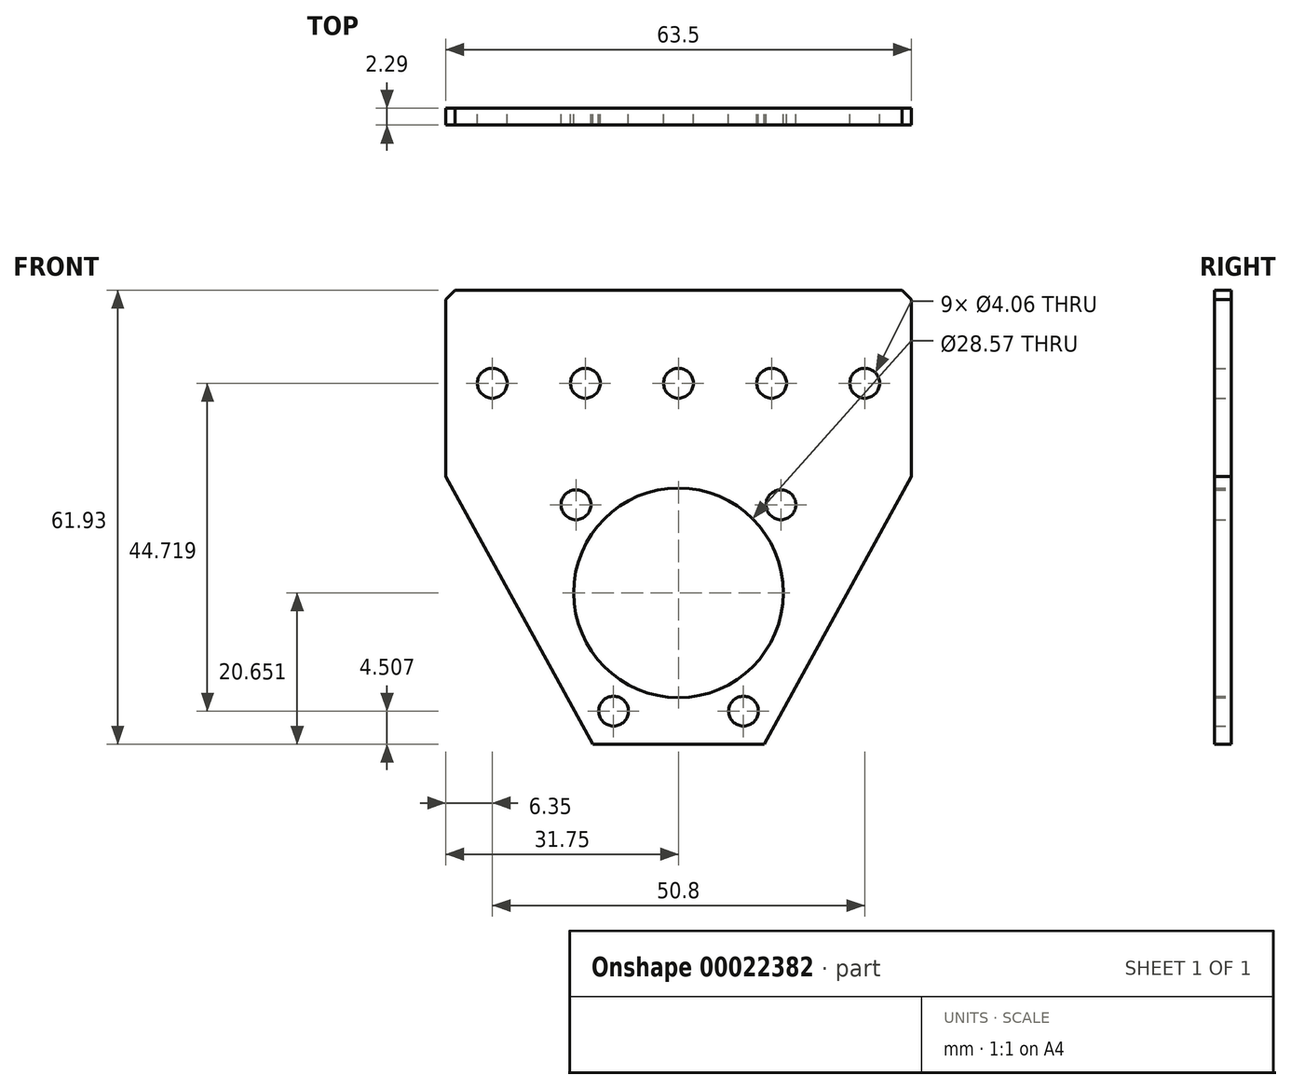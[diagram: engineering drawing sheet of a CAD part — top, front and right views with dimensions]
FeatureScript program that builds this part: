
annotation { "Feature Type Name" : "Feature", "Feature Type Description" : "" }
export const myFeature = defineFeature(function(context is Context, id is Id, definition is map)
    precondition{}
    {
        {
            var Q0;
            Q0=qCreatedBy(makeId("Front.planeOp"),FACE);
            var sketch = newSketch(context, id + "F0", { "sketchPlane" : qUnion([Q0])});
            skLineSegment(sketch, "E0.bottom", {"start": v(-31.75, 16.43) * mm, "end": v(31.75, 16.43) * mm});
            skLineSegment(sketch, "E0.top", {"start": v(-11.7, -45.5) * mm, "end": v(11.7, -45.5) * mm});
            skLineSegment(sketch, "E0.left", {"start": v(-31.75, 16.43) * mm, "end": v(-31.75, -8.97) * mm});
            skLineSegment(sketch, "E0.right", {"start": v(31.75, 16.43) * mm, "end": v(31.75, -8.97) * mm});
            skLineSegment(sketch, "E1", {"start": v(-31.75, -8.97) * mm, "end": v(-11.7, -45.5) * mm});
            skLineSegment(sketch, "E2", {"start": v(31.75, -8.97) * mm, "end": v(11.7, -45.5) * mm});
            skLineSegment(sketch, "E3", {"start": v(31.75, 3.73) * mm, "end": v(-31.75, 3.73) * mm, "construction": true});
            skCircle(sketch, "E4", {"center": v(0, -24.85) * mm, "radius": 14.29 * mm});
            skSolve(sketch);
        }
        {
            var Q0;
            Q0=makeQuery(id+"F0.imprint","IMPRINT",FACE,{"disambiguationData":[TD([[makeQuery(id+"F0.imprint","IMPRINT",EDGE,{"derivedFrom":sQuery(id+"F0.wireOp",EDGE,"E0.bottom")}),-1.0]])]});
            extrude(context, id + "F1", {"entities" : qUnion([Q0]), "depth" : 2.3 * mm});
        }
        {
            var Q0;
            Q0=makeQuery(id+"F1.opExtrude","CAP_FACE",FACE,{"disambiguationData":[OSD([sQuery(id+"F0.wireOp",EDGE,"E0.bottom"),sQuery(id+"F0.wireOp",EDGE,"E0.top"),sQuery(id+"F0.wireOp",EDGE,"E0.left"),sQuery(id+"F0.wireOp",EDGE,"E0.right"),sQuery(id+"F0.wireOp",EDGE,"dd962b13-b751-4e5a-9dd1-f75176092dec"),sQuery(id+"F0.wireOp",EDGE,"E1"),sQuery(id+"F0.wireOp",EDGE,"E2")])],"isStart":true});
            var sketch = newSketch(context, id + "F2", { "sketchPlane" : qUnion([Q0])});
            skLineSegment(sketch, "E5.bottom", {"start": v(-25.4, 3.73) * mm, "end": v(25.4, 3.73) * mm});
            skLineSegment(sketch, "E5.top", {"start": v(-25.4, -45.5) * mm, "end": v(25.4, -45.5) * mm});
            skLineSegment(sketch, "E5.left", {"start": v(-25.4, 3.73) * mm, "end": v(-25.4, -45.5) * mm});
            skLineSegment(sketch, "E5.right", {"start": v(25.4, 3.73) * mm, "end": v(25.4, -45.5) * mm});
            skLineSegment(sketch, "E6", {"start": v(0, 16.43) * mm, "end": v(0, -45.5) * mm});
            skPoint(sketch, "E7", {"position": v(12.7, 3.73) * mm});
            skPoint(sketch, "E8", {"position": v(0, 3.73) * mm});
            skPoint(sketch, "E9", {"position": v(-12.7, 3.73) * mm});
            skSolve(sketch);
        }
        {
            var Q0;
            Q0=sQuery(id+"F2.wireOp",VERTEX,"E5.right.start");
            var Q1;
            Q1=sQuery(id+"F2.wireOp",VERTEX,"E7");
            var Q2;
            Q2=sQuery(id+"F2.wireOp",VERTEX,"E8");
            var Q3;
            Q3=sQuery(id+"F2.wireOp",VERTEX,"E9");
            var Q4;
            Q4=sQuery(id+"F2.wireOp",VERTEX,"E5.left.start");
            var Q5;
            Q5=makeQuery(id+"F1.opExtrude","SWEPT_BODY",BODY,{"disambiguationData":[OSD([sQuery(id+"F0.wireOp",EDGE,"E0.bottom"),sQuery(id+"F0.wireOp",EDGE,"E0.top"),sQuery(id+"F0.wireOp",EDGE,"E0.left"),sQuery(id+"F0.wireOp",EDGE,"E0.right"),sQuery(id+"F0.wireOp",EDGE,"dd962b13-b751-4e5a-9dd1-f75176092dec"),sQuery(id+"F0.wireOp",EDGE,"E1"),sQuery(id+"F0.wireOp",EDGE,"E2")])]});
            hole(context, id + "F3", {"style" : HoleStyle.SIMPLE, "holeDiameter" : 4.06 * mm, "endStyle" : HoleEndStyle.THROUGH, "locations" : qUnion([Q0, Q1, Q2, Q3, Q4]), "scope" : qUnion([Q5])});
        }
        {
            var Q0;
            Q0=makeQuery(id+"F1.opExtrude","CAP_FACE",FACE,{"disambiguationData":[OSD([sQuery(id+"F0.wireOp",EDGE,"E0.bottom"),sQuery(id+"F0.wireOp",EDGE,"E0.top"),sQuery(id+"F0.wireOp",EDGE,"E0.left"),sQuery(id+"F0.wireOp",EDGE,"E0.right"),sQuery(id+"F0.wireOp",EDGE,"E1"),sQuery(id+"F0.wireOp",EDGE,"E2"),sQuery(id+"F0.wireOp",EDGE,"E4")])],"isStart":true});
            var sketch = newSketch(context, id + "F4", { "sketchPlane" : qUnion([Q0])});
            skCircle(sketch, "E10", {"center": v(0, -24.85) * mm, "radius": 18.41 * mm});
            skPoint(sketch, "E11", {"position": v(-13.97, -12.86) * mm});
            skPoint(sketch, "E12", {"position": v(13.97, -12.86) * mm});
            skPoint(sketch, "E13", {"position": v(8.86, -41) * mm});
            skPoint(sketch, "E14", {"position": v(-8.86, -41) * mm});
            skSolve(sketch);
        }
        {
            var Q0;
            Q0=sQuery(id+"F4.wireOp",VERTEX,"E11");
            var Q1;
            Q1=sQuery(id+"F4.wireOp",VERTEX,"E12");
            var Q2;
            Q2=sQuery(id+"F4.wireOp",VERTEX,"E13");
            var Q3;
            Q3=sQuery(id+"F4.wireOp",VERTEX,"E14");
            var Q4;
            Q4=makeQuery(id+"F1.opExtrude","SWEPT_BODY",BODY,{"disambiguationData":[OSD([sQuery(id+"F0.wireOp",EDGE,"E0.bottom"),sQuery(id+"F0.wireOp",EDGE,"E0.top"),sQuery(id+"F0.wireOp",EDGE,"E0.left"),sQuery(id+"F0.wireOp",EDGE,"E0.right"),sQuery(id+"F0.wireOp",EDGE,"E1"),sQuery(id+"F0.wireOp",EDGE,"E2"),sQuery(id+"F0.wireOp",EDGE,"E4")])]});
            hole(context, id + "F5", {"style" : HoleStyle.SIMPLE, "holeDiameter" : 4.06 * mm, "endStyle" : HoleEndStyle.THROUGH, "locations" : qUnion([Q0, Q1, Q2, Q3]), "scope" : qUnion([Q4])});
        }
        {
            var Q0;
            Q0=makeQuery(id+"F1.opExtrude","SWEPT_EDGE",EDGE,{"disambiguationData":[OSD([sQuery(id+"F0.wireOp",EDGE,"E0.bottom"),sQuery(id+"F0.wireOp",EDGE,"E0.right")])]});
            var Q1;
            Q1=makeQuery(id+"F1.opExtrude","SWEPT_EDGE",EDGE,{"disambiguationData":[OSD([sQuery(id+"F0.wireOp",EDGE,"E0.bottom"),sQuery(id+"F0.wireOp",EDGE,"E0.left")])]});
            chamfer(context, id + "F6", {"entities" : qUnion([Q0, Q1]), "width" : 1.27 * mm, "tangentPropagation" : true});
        }
    });
